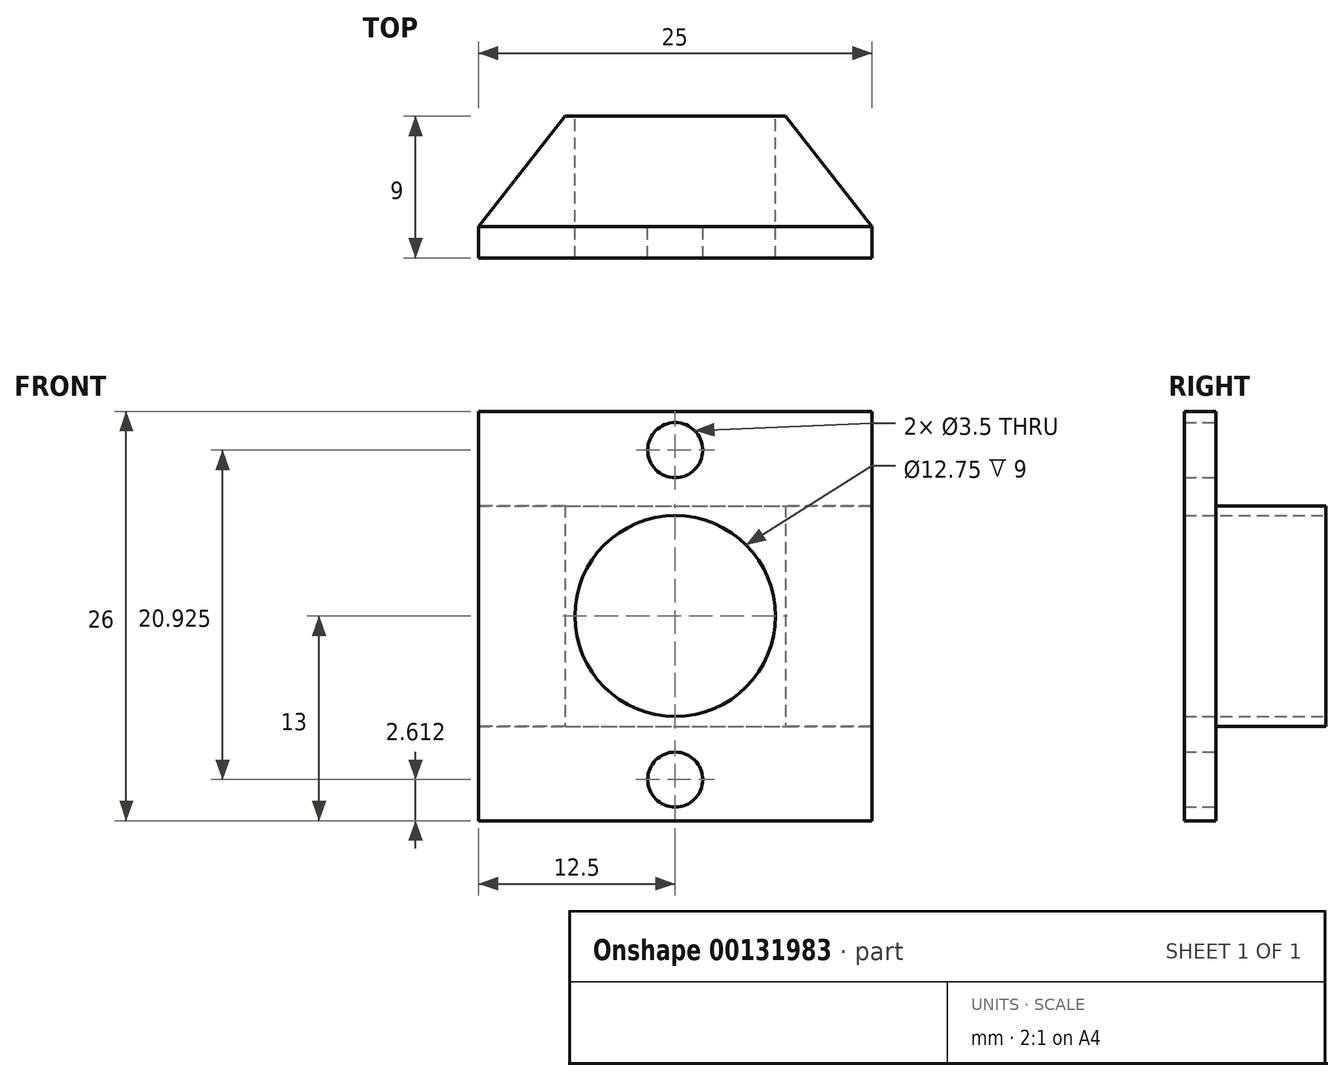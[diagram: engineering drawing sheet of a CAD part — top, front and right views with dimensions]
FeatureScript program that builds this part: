
annotation { "Feature Type Name" : "Feature", "Feature Type Description" : "" }
export const myFeature = defineFeature(function(context is Context, id is Id, definition is map)
    precondition{}
    {
        {
            var Q0;
            Q0=qCreatedBy(makeId("Top.planeOp"),FACE);
            var sketch = newSketch(context, id + "F0", { "sketchPlane" : qUnion([Q0])});
            skLineSegment(sketch, "E0", {"start": v(0, 0) * mm, "end": v(-12.5, 0) * mm});
            skLineSegment(sketch, "E1", {"start": v(0, 7) * mm, "end": v(-7, 7) * mm});
            skLineSegment(sketch, "E2", {"start": v(-7, 7) * mm, "end": v(-12.5, 0) * mm});
            skLineSegment(sketch, "E3", {"start": v(12.5, 0) * mm, "end": v(7, 7) * mm});
            skLineSegment(sketch, "E4", {"start": v(0, 7) * mm, "end": v(7, 7) * mm});
            skLineSegment(sketch, "E5", {"start": v(0, 0) * mm, "end": v(12.5, 0) * mm});
            skLineSegment(sketch, "E6", {"start": v(-12.5, 0) * mm, "end": v(-12.5, -2) * mm});
            skLineSegment(sketch, "E7", {"start": v(12.5, -2) * mm, "end": v(12.5, 0) * mm});
            skLineSegment(sketch, "E8", {"start": v(12.5, -2) * mm, "end": v(-12.5, -2) * mm});
            skSolve(sketch);
        }
        {
            var Q0;
            Q0 = qSketchRegion(id + "F0", true);
            var Q1;
            Q1=makeQuery(id+"F0.imprint","IMPRINT",FACE,{"disambiguationData":[TD([[makeQuery(id+"F0.imprint","IMPRINT",EDGE,{"derivedFrom":sQuery(id+"F0.wireOp",EDGE,"E0")}),-1.0]])]});
            extrude(context, id + "F1", {"entities" : qUnion([Q0, Q1]), "depth" : 14 * mm});
        }
        {
            var Q0;
            Q0=makeQuery(id+"F1.opExtrude","SWEPT_FACE",FACE,{"disambiguationData":[OSD([sQuery(id+"F0.wireOp",EDGE,"E1"),sQuery(id+"F0.wireOp",EDGE,"E4")])]});
            var sketch = newSketch(context, id + "F2", { "sketchPlane" : qUnion([Q0])});
            skPoint(sketch, "E9", {"position": v(0, 7) * mm});
            skSolve(sketch);
        }
        {
            var Q0;
            Q0=makeQuery(id+"F1.opExtrude","CAP_FACE",FACE,{"disambiguationData":[OSD([sQuery(id+"F0.wireOp",EDGE,"E1"),sQuery(id+"F0.wireOp",EDGE,"E2"),sQuery(id+"F0.wireOp",EDGE,"E3"),sQuery(id+"F0.wireOp",EDGE,"E4"),sQuery(id+"F0.wireOp",EDGE,"E6"),sQuery(id+"F0.wireOp",EDGE,"E7"),sQuery(id+"F0.wireOp",EDGE,"E8")])],"isStart":true});
            var sketch = newSketch(context, id + "F3", { "sketchPlane" : qUnion([Q0])});
            skLineSegment(sketch, "E10", {"start": v(-12.5, 0) * mm, "end": v(12.5, 0) * mm});
            skLineSegment(sketch, "E11", {"start": v(12.5, 0) * mm, "end": v(12.5, 2) * mm});
            skLineSegment(sketch, "E12", {"start": v(12.5, 2) * mm, "end": v(-12.5, 2) * mm});
            skLineSegment(sketch, "E13", {"start": v(-12.5, 2) * mm, "end": v(-12.5, 0) * mm});
            skSolve(sketch);
        }
        {
            var Q0;
            Q0=makeQuery(id+"F3.imprint","IMPRINT",FACE,{"disambiguationData":[TD([[makeQuery(id+"F3.imprint","IMPRINT",EDGE,{"derivedFrom":sQuery(id+"F3.wireOp",EDGE,"E10")}),1.0]])]});
            extrude(context, id + "F4", {"entities" : qUnion([Q0]), "operationType" : NewBodyOperationType.ADD, "depth" : 6 * mm});
        }
        {
            var Q0;
            Q0=makeQuery(id+"F1.opExtrude","CAP_FACE",FACE,{"disambiguationData":[OSD([sQuery(id+"F0.wireOp",EDGE,"E1"),sQuery(id+"F0.wireOp",EDGE,"E2"),sQuery(id+"F0.wireOp",EDGE,"E3"),sQuery(id+"F0.wireOp",EDGE,"E4"),sQuery(id+"F0.wireOp",EDGE,"E6"),sQuery(id+"F0.wireOp",EDGE,"E7"),sQuery(id+"F0.wireOp",EDGE,"E8")])],"isStart":false});
            var sketch = newSketch(context, id + "F5", { "sketchPlane" : qUnion([Q0])});
            skLineSegment(sketch, "E14.bottom", {"start": v(-12.5, -2) * mm, "end": v(12.5, -2) * mm});
            skLineSegment(sketch, "E14.top", {"start": v(-12.5, 0) * mm, "end": v(12.5, 0) * mm});
            skLineSegment(sketch, "E14.left", {"start": v(-12.5, -2) * mm, "end": v(-12.5, 0) * mm});
            skLineSegment(sketch, "E14.right", {"start": v(12.5, -2) * mm, "end": v(12.5, 0) * mm});
            skSolve(sketch);
        }
        {
            var Q0;
            Q0=makeQuery(id+"F5.imprint","IMPRINT",FACE,{"disambiguationData":[TD([[makeQuery(id+"F5.imprint","IMPRINT",EDGE,{"derivedFrom":sQuery(id+"F5.wireOp",EDGE,"E14.bottom")}),-1.0]])]});
            extrude(context, id + "F6", {"entities" : qUnion([Q0]), "operationType" : NewBodyOperationType.ADD, "depth" : 6 * mm});
        }
        {
            var Q0;
            Q0=makeQuery(id+"F4.opExtrude","SWEPT_FACE",FACE,{"disambiguationData":[OSD([sQuery(id+"F3.wireOp",EDGE,"E10")])]});
            var sketch = newSketch(context, id + "F7", { "sketchPlane" : qUnion([Q0])});
            skPoint(sketch, "E15", {"position": v(0, -3.39) * mm});
            skPoint(sketch, "E15.positionSnap0", {"position": v(0, -6) * mm});
            skSolve(sketch);
        }
        {
            var Q0;
            Q0=sQuery(id+"F7.wireOp",VERTEX,"E15");
            var Q1;
            Q1=makeQuery(id+"F1.opExtrude","SWEPT_BODY",BODY,{"disambiguationData":[OSD([sQuery(id+"F0.wireOp",EDGE,"E1"),sQuery(id+"F0.wireOp",EDGE,"E2"),sQuery(id+"F0.wireOp",EDGE,"E3"),sQuery(id+"F0.wireOp",EDGE,"E4"),sQuery(id+"F0.wireOp",EDGE,"E6"),sQuery(id+"F0.wireOp",EDGE,"E7"),sQuery(id+"F0.wireOp",EDGE,"E8")])]});
            hole(context, id + "F8", {"style" : HoleStyle.SIMPLE, "endStyle" : HoleEndStyle.THROUGH, "holeDiameter" : 3.5 * mm, "locations" : qUnion([Q0]), "scope" : qUnion([Q1]), "isTappedThrough" : true});
        }
        {
            var Q0;
            Q0=makeQuery(id+"F6.opExtrude","SWEPT_FACE",FACE,{"disambiguationData":[OSD([sQuery(id+"F5.wireOp",EDGE,"E14.top")])]});
            var sketch = newSketch(context, id + "F9", { "sketchPlane" : qUnion([Q0])});
            skPoint(sketch, "E16", {"position": v(0, 17.54) * mm});
            skPoint(sketch, "E16.positionSnap0", {"position": v(0, 20) * mm});
            skSolve(sketch);
        }
        {
            var Q0;
            Q0=sQuery(id+"F9.wireOp",VERTEX,"E16");
            var Q1;
            Q1=makeQuery(id+"F1.opExtrude","SWEPT_BODY",BODY,{"disambiguationData":[OSD([sQuery(id+"F0.wireOp",EDGE,"E1"),sQuery(id+"F0.wireOp",EDGE,"E2"),sQuery(id+"F0.wireOp",EDGE,"E3"),sQuery(id+"F0.wireOp",EDGE,"E4"),sQuery(id+"F0.wireOp",EDGE,"E6"),sQuery(id+"F0.wireOp",EDGE,"E7"),sQuery(id+"F0.wireOp",EDGE,"E8")])]});
            hole(context, id + "F10", {"style" : HoleStyle.SIMPLE, "endStyle" : HoleEndStyle.THROUGH, "holeDiameter" : 3.5 * mm, "locations" : qUnion([Q0]), "scope" : qUnion([Q1]), "isTappedThrough" : true});
        }
        {
            var Q0;
            Q0=sQuery(id+"F2.wireOp",VERTEX,"E9");
            var Q1;
            Q1=makeQuery(id+"F1.opExtrude","SWEPT_BODY",BODY,{"disambiguationData":[OSD([sQuery(id+"F0.wireOp",EDGE,"E1"),sQuery(id+"F0.wireOp",EDGE,"E2"),sQuery(id+"F0.wireOp",EDGE,"E3"),sQuery(id+"F0.wireOp",EDGE,"E4"),sQuery(id+"F0.wireOp",EDGE,"E6"),sQuery(id+"F0.wireOp",EDGE,"E7"),sQuery(id+"F0.wireOp",EDGE,"E8")])]});
            hole(context, id + "F11", {"style" : HoleStyle.SIMPLE, "endStyle" : HoleEndStyle.THROUGH, "holeDiameter" : 12.75 * mm, "locations" : qUnion([Q0]), "scope" : qUnion([Q1]), "isTappedThrough" : true});
        }
    });
